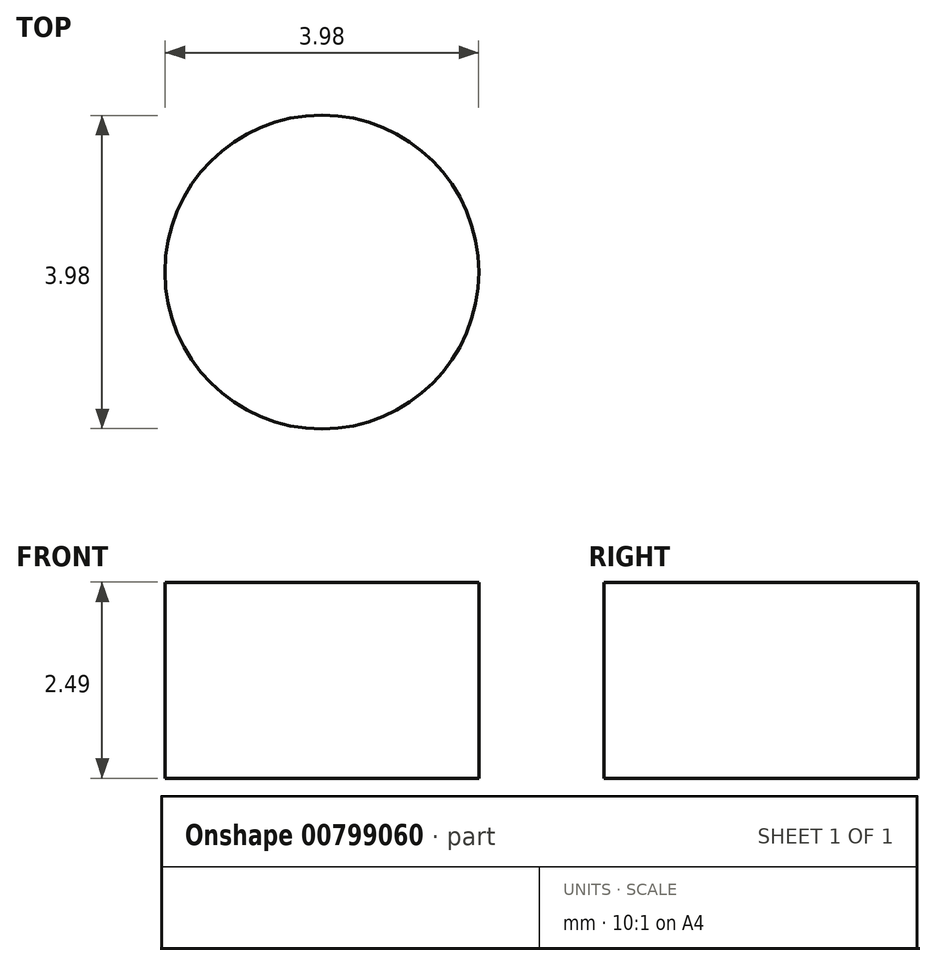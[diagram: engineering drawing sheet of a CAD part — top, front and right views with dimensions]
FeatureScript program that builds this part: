
annotation { "Feature Type Name" : "Feature", "Feature Type Description" : "" }
export const myFeature = defineFeature(function(context is Context, id is Id, definition is map)
    precondition{}
    {
        {
            var Q0;
            Q0=qCreatedBy(makeId("Top.planeOp"),FACE);
            var sketch = newSketch(context, id + "F0", { "sketchPlane" : qUnion([Q0])});
            skCircle(sketch, "E0", {"center": v(0, 0) * mm, "radius": 2 * mm});
            skSolve(sketch);
        }
        {
            var Q0;
            Q0=makeQuery(id+"F0.imprint","IMPRINT",FACE,{"disambiguationData":[TD([[makeQuery(id+"F0.imprint","IMPRINT",EDGE,{"derivedFrom":sQuery(id+"F0.wireOp",EDGE,"E0")}),1.0]])]});
            var Q1;
            Q1=sQuery(id+"F0.wireOp",EDGE,"E0");
            extrude(context, id + "F1", {"entities" : qUnion([Q0]), "surfaceEntities" : qUnion([Q1]), "depth" : 2.5 * mm, "offsetDistance" : 25.4 * mm});
        }
    });
